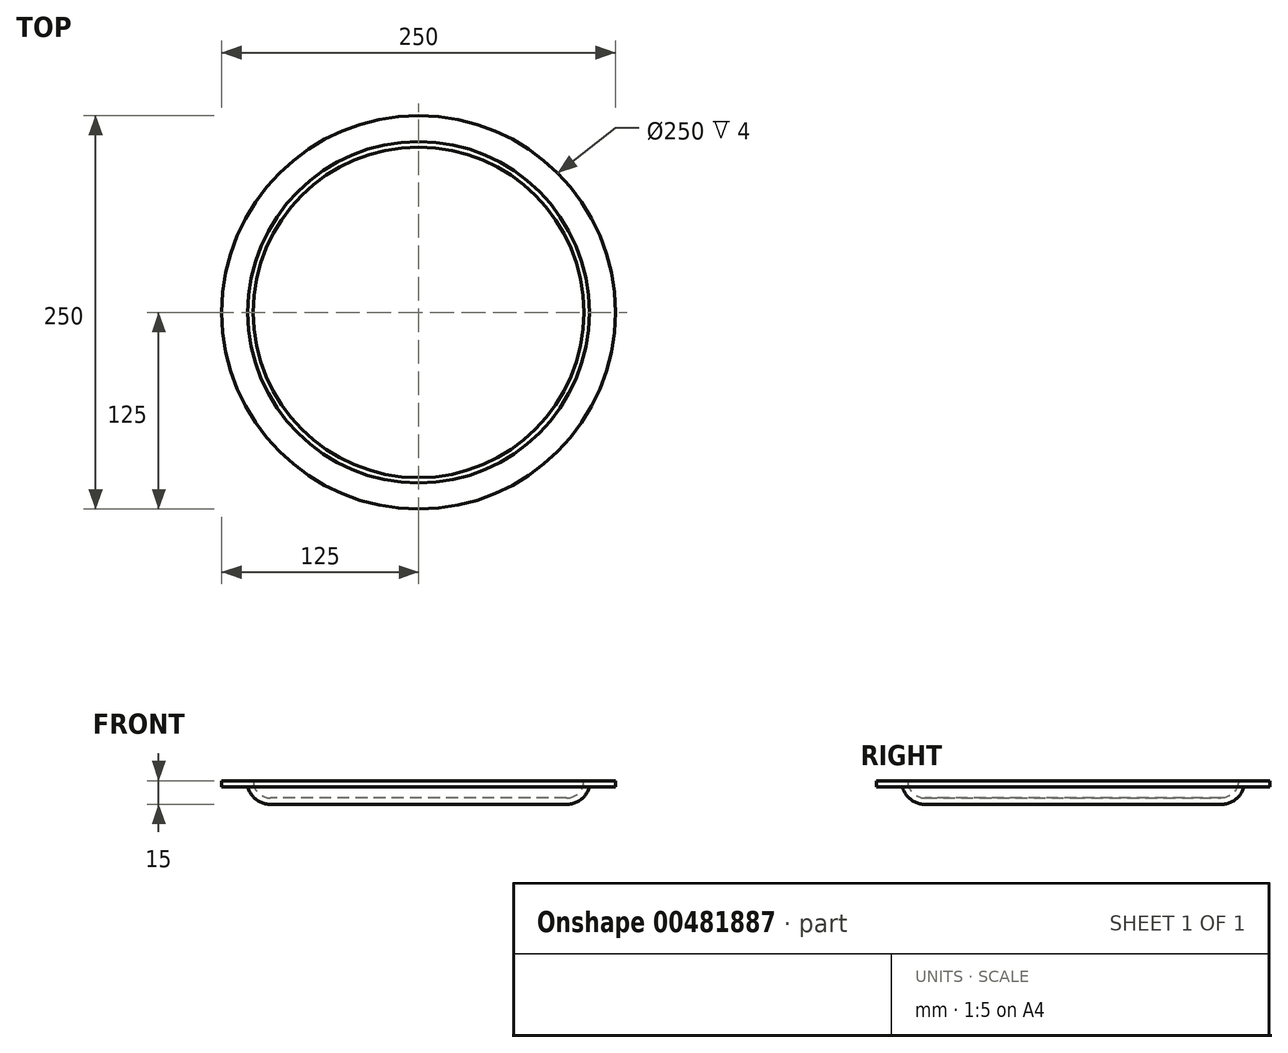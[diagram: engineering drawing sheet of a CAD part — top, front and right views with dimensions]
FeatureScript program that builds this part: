
annotation { "Feature Type Name" : "Feature", "Feature Type Description" : "" }
export const myFeature = defineFeature(function(context is Context, id is Id, definition is map)
    precondition{}
    {
        {
            var Q0;
            Q0=qCreatedBy(makeId("Front.planeOp"),FACE);
            var sketch = newSketch(context, id + "F0", { "sketchPlane" : qUnion([Q0])});
            skLineSegment(sketch, "E0", {"start": v(0, 0) * mm, "end": v(-94, 0) * mm});
            skArc(sketch, "E1", {"start": v(-94, 0) * mm, "mid": v(-103.08, 3.06) * mm, "end": v(-108.46, 11) * mm});
            skLineSegment(sketch, "E2", {"start": v(-108.46, 11) * mm, "end": v(-125, 11) * mm});
            skLineSegment(sketch, "E3", {"start": v(-125, 11) * mm, "end": v(-125, 15) * mm});
            skLineSegment(sketch, "E4", {"start": v(-125, 15) * mm, "end": v(-105, 15) * mm});
            skArc(sketch, "E5", {"start": v(-105, 15) * mm, "mid": v(-101.78, 7.22) * mm, "end": v(-94, 4) * mm});
            skLineSegment(sketch, "E6", {"start": v(-94, 4) * mm, "end": v(0, 4) * mm});
            skLineSegment(sketch, "E7", {"start": v(0, 0) * mm, "end": v(0, 21.65) * mm, "construction": true});
            skLineSegment(sketch, "E8", {"start": v(0, 0) * mm, "end": v(0, 4) * mm});
            skSolve(sketch);
        }
        {
            var Q0;
            Q0=sQuery(id+"F0.wireOp",EDGE,"E0");
            var Q1;
            Q1=sQuery(id+"F0.wireOp",EDGE,"E6");
            var Q2;
            Q2=sQuery(id+"F0.wireOp",EDGE,"E1");
            var Q3;
            Q3=sQuery(id+"F0.wireOp",EDGE,"E5");
            var Q4;
            Q4=sQuery(id+"F0.wireOp",EDGE,"E4");
            var Q5;
            Q5=sQuery(id+"F0.wireOp",EDGE,"E2");
            var Q6;
            Q6=sQuery(id+"F0.wireOp",EDGE,"E3");
            var Q7;
            Q7=sQuery(id+"F0.wireOp",EDGE,"E7");
            revolve(context, id + "F1", {"bodyType" : ToolBodyType.SURFACE, "surfaceEntities" : qUnion([Q0, Q1, Q2, Q3, Q4, Q5, Q6]), "axis" : qUnion([Q7]), "revolveType" : RevolveType.FULL});
        }
    });
